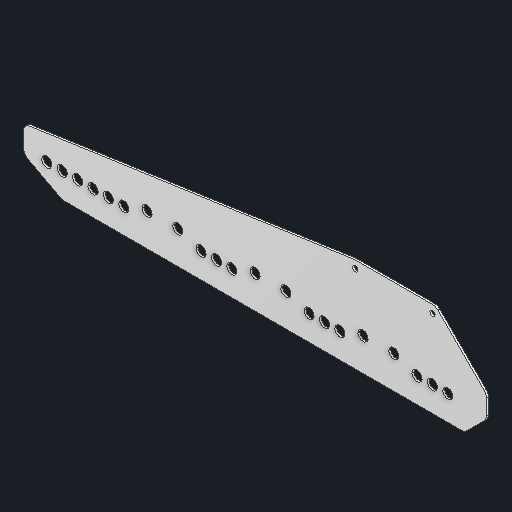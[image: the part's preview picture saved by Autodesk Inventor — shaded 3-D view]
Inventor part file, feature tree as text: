
AUTODESK INVENTOR PART (.ipt)
format: ipt  version: 2025 (Build 290162000, 162)  size: 160,768 bytes
history: native  units: in
note: dims shown in document units (in); Inventor stores cm internally (conversion verified against a paired STEP export)
features: other x3, extrude x1, sketch x1
ambient origin geometry x8: Origin, YZ Plane, XZ Plane, XY Plane, X Axis, Y Axis, Z Axis, Center Point
bodies: Solid1 (feature_tree)
feature tree (5):
  other  "Blocks"
  extrude  "Extrusion1"  Depth=0.0625in
  sketch  "Sketch1"  dims[d0=135.0deg d1=135.0deg d2=0.25in d3=0.125in d4=0.332in d5=0.332in d6=0.0625in d7=0.0in]
  other  "main"
  other  "main:1"
